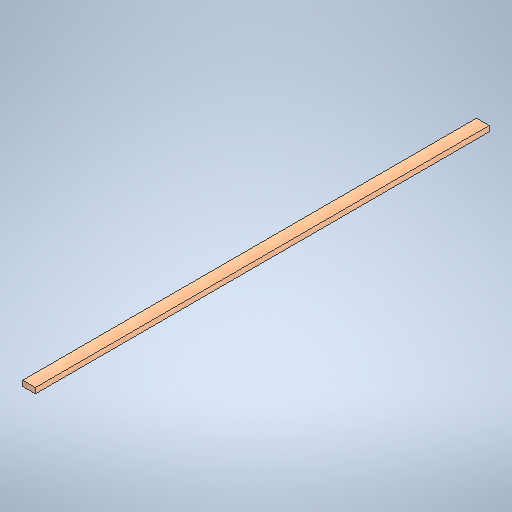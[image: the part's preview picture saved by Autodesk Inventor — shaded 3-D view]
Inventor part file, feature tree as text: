
AUTODESK INVENTOR PART (.ipt)
format: ipt  version: 2025 (Build 290162010, 162A)  size: 269,824 bytes
history: native  units: in
note: dims shown in document units (in); Inventor stores cm internally (conversion verified against a paired STEP export)
features: extrude x1, sketch x1
ambient origin geometry x8: Origin, YZ Plane, XZ Plane, XY Plane, X Axis, Y Axis, Z Axis, Center Point
bodies: Solid1 (feature_tree)
feature tree (2):
  extrude  "Extrusion1"  Depth=1.5in
  sketch  "Sketch1"  dims[d0=3.5in d1=1.5in d2=125.0in d3=0.0in]
